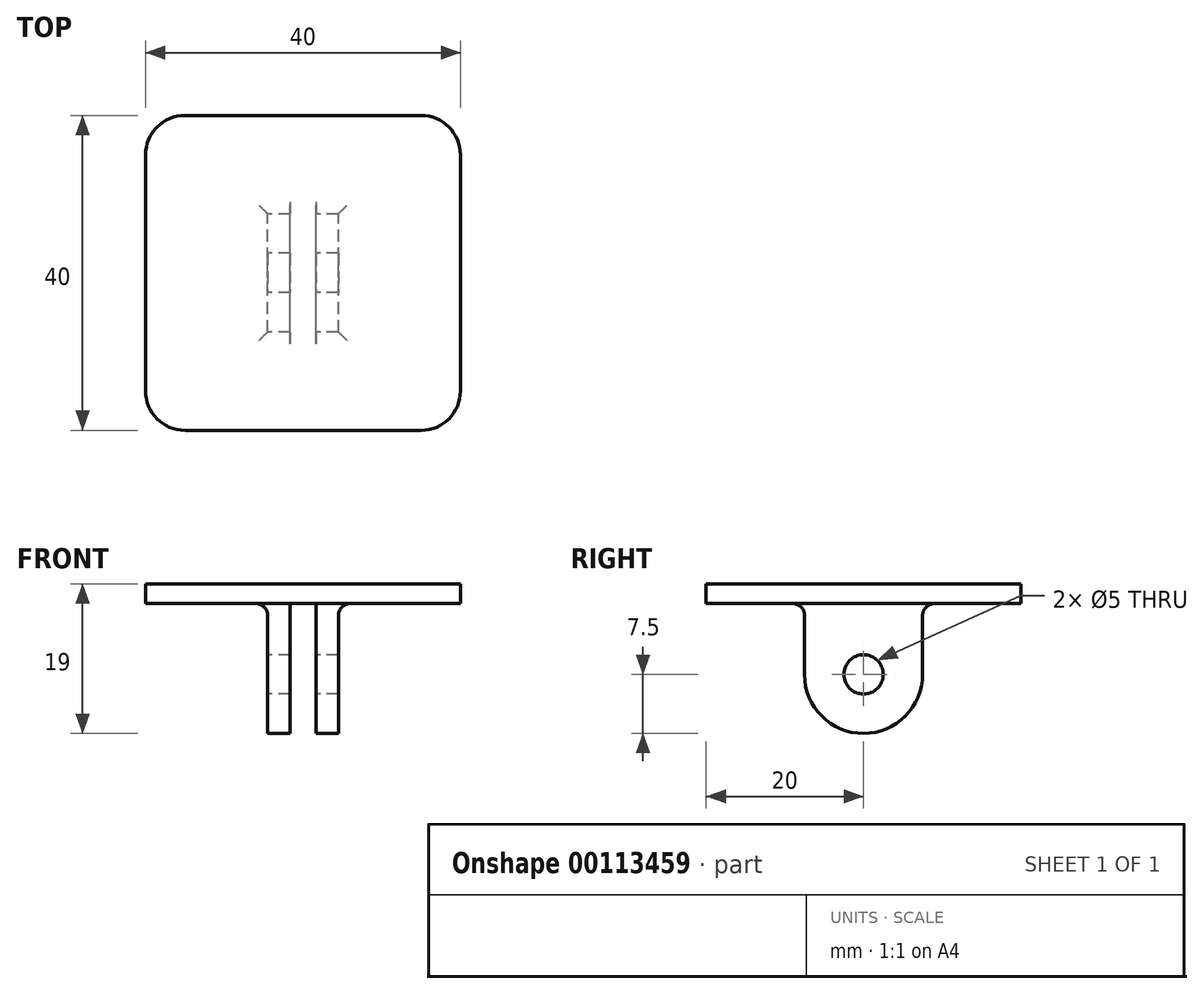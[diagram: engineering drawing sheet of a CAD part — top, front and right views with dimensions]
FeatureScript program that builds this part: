
annotation { "Feature Type Name" : "Feature", "Feature Type Description" : "" }
export const myFeature = defineFeature(function(context is Context, id is Id, definition is map)
    precondition{}
    {
        {
            var Q0;
            Q0=qCreatedBy(makeId("Right.planeOp"),FACE);
            var sketch = newSketch(context, id + "F0", { "sketchPlane" : qUnion([Q0])});
            skArc(sketch, "E0", {"start": v(-7.5, 0) * mm, "mid": v(0, -7.5) * mm, "end": v(7.5, 0) * mm});
            skLineSegment(sketch, "E1", {"start": v(-7.5, 0) * mm, "end": v(-7.5, 9) * mm});
            skLineSegment(sketch, "E2", {"start": v(-7.5, 9) * mm, "end": v(-20, 9) * mm});
            skLineSegment(sketch, "E3", {"start": v(-20, 9) * mm, "end": v(-20, 11.5) * mm});
            skLineSegment(sketch, "E4", {"start": v(-20, 11.5) * mm, "end": v(20, 11.5) * mm});
            skLineSegment(sketch, "E5", {"start": v(7.5, 0) * mm, "end": v(7.5, 9) * mm});
            skLineSegment(sketch, "E6", {"start": v(7.5, 9) * mm, "end": v(20, 9) * mm});
            skLineSegment(sketch, "E7", {"start": v(20, 9) * mm, "end": v(20, 11.5) * mm});
            skCircle(sketch, "E8", {"center": v(0, 0) * mm, "radius": 2.5 * mm});
            skLineSegment(sketch, "E9", {"start": v(-7.5, 9) * mm, "end": v(7.5, 9) * mm});
            skSolve(sketch);
        }
        {
            var Q0;
            Q0 = qSketchRegion(id + "F0", true);
            extrude(context, id + "F1", {"entities" : qUnion([Q0]), "endBound" : BoundingType.SYMMETRIC, "depth" : 9 * mm});
        }
        {
            var Q0;
            Q0=makeQuery(id+"F0.imprint","IMPRINT",FACE,{"disambiguationData":[TD([[makeQuery(id+"F0.imprint","IMPRINT",EDGE,{"derivedFrom":sQuery(id+"F0.wireOp",EDGE,"E2")}),-1.0]])]});
            extrude(context, id + "F2", {"entities" : qUnion([Q0]), "operationType" : NewBodyOperationType.ADD, "endBound" : BoundingType.SYMMETRIC, "depth" : 40 * mm});
        }
        {
            var Q0;
            {var subQ0=sQuery(id+"F0.wireOp",EDGE,"E6");var subQ1=sQuery(id+"F0.wireOp",EDGE,"E2");Q0=makeQuery(id+"F2.boolean.opBoolean","MERGE",FACE,{"derivedFrom":[makeQuery(id+"F1.opExtrude","SWEPT_FACE",FACE,{"disambiguationData":[OSD([subQ1])]}),makeQuery(id+"F1.opExtrude","SWEPT_FACE",FACE,{"disambiguationData":[OSD([subQ0])]}),makeQuery(id+"F2.opExtrude","SWEPT_FACE",FACE,{"disambiguationData":[OSD([subQ1,subQ0,sQuery(id+"F0.wireOp",EDGE,"E9")])]})]});}
            var sketch = newSketch(context, id + "F3", { "sketchPlane" : qUnion([Q0])});
            skLineSegment(sketch, "E10.bottom", {"start": v(1.63, 10) * mm, "end": v(-1.62, 10) * mm});
            skLineSegment(sketch, "E10.top", {"start": v(1.63, -10) * mm, "end": v(-1.63, -10) * mm});
            skLineSegment(sketch, "E10.left", {"start": v(1.63, 10) * mm, "end": v(1.63, -10) * mm});
            skLineSegment(sketch, "E10.right", {"start": v(-1.62, 10) * mm, "end": v(-1.63, -10) * mm});
            skPoint(sketch, "E10.middle", {"position": v(0, 0) * mm});
            skSolve(sketch);
        }
        {
            var Q0;
            Q0 = qSketchRegion(id + "F3", true);
            extrude(context, id + "F4", {"entities" : qUnion([Q0]), "operationType" : NewBodyOperationType.REMOVE, "depth" : 25 * mm});
        }
        {
            var Q0;
            {var subQ0=sQuery(id+"F0.wireOp",EDGE,"E6");var subQ1=sQuery(id+"F0.wireOp",EDGE,"E2");Q0=makeQuery(id+"F2.boolean.opBoolean","INTERSECT",EDGE,{"derivedFrom":[makeQuery(id+"F1.opExtrude","CAP_FACE",FACE,{"disambiguationData":[OSD([sQuery(id+"F0.wireOp",EDGE,"E0"),sQuery(id+"F0.wireOp",EDGE,"E1"),subQ1,sQuery(id+"F0.wireOp",EDGE,"E3"),sQuery(id+"F0.wireOp",EDGE,"E4"),sQuery(id+"F0.wireOp",EDGE,"E5"),subQ0,sQuery(id+"F0.wireOp",EDGE,"E7"),sQuery(id+"F0.wireOp",EDGE,"E8")])],"isStart":true}),makeQuery(id+"F2.opExtrude","SWEPT_FACE",FACE,{"disambiguationData":[OSD([subQ1,subQ0,sQuery(id+"F0.wireOp",EDGE,"E9")])]})]});}
            var Q1;
            {var subQ0=sQuery(id+"F0.wireOp",EDGE,"E6");var subQ1=sQuery(id+"F0.wireOp",EDGE,"E2");Q1=makeQuery(id+"F2.boolean.opBoolean","INTERSECT",EDGE,{"derivedFrom":[makeQuery(id+"F1.opExtrude","CAP_FACE",FACE,{"disambiguationData":[OSD([sQuery(id+"F0.wireOp",EDGE,"E0"),sQuery(id+"F0.wireOp",EDGE,"E1"),subQ1,sQuery(id+"F0.wireOp",EDGE,"E3"),sQuery(id+"F0.wireOp",EDGE,"E4"),sQuery(id+"F0.wireOp",EDGE,"E5"),subQ0,sQuery(id+"F0.wireOp",EDGE,"E7"),sQuery(id+"F0.wireOp",EDGE,"E8")])],"isStart":false}),makeQuery(id+"F2.opExtrude","SWEPT_FACE",FACE,{"disambiguationData":[OSD([subQ1,subQ0,sQuery(id+"F0.wireOp",EDGE,"E9")])]})]});}
            var Q2;
            {var subQ0=sQuery(id+"F0.wireOp",EDGE,"E6");var subQ1=sQuery(id+"F0.wireOp",EDGE,"E5");var subQ3=sQuery(id+"F0.wireOp",EDGE,"E9");var subQ4=sQuery(id+"F3.wireOp",EDGE,"E10.right");Q2=makeQuery(id+"F4.boolean.opBoolean","SPLIT",EDGE,{"disambiguationData":[TD([makeQuery(id+"F4.opExtrude","SWEPT_FACE",FACE,{"disambiguationData":[OSD([subQ4])]})])],"derivedFrom":makeQuery(id+"F1.opExtrude","SWEPT_EDGE",EDGE,{"disambiguationData":[OSD([subQ1,subQ0,subQ3])]})});}
            var Q3;
            {var subQ0=sQuery(id+"F0.wireOp",EDGE,"E5");var subQ2=sQuery(id+"F0.wireOp",EDGE,"E6");var subQ3=sQuery(id+"F0.wireOp",EDGE,"E9");var subQ4=sQuery(id+"F3.wireOp",EDGE,"E10.left");Q3=makeQuery(id+"F4.boolean.opBoolean","SPLIT",EDGE,{"disambiguationData":[TD([makeQuery(id+"F4.opExtrude","SWEPT_FACE",FACE,{"disambiguationData":[OSD([subQ4])]})])],"derivedFrom":makeQuery(id+"F1.opExtrude","SWEPT_EDGE",EDGE,{"disambiguationData":[OSD([subQ0,subQ2,subQ3])]})});}
            var Q4;
            {var subQ0=sQuery(id+"F0.wireOp",EDGE,"E2");var subQ2=sQuery(id+"F0.wireOp",EDGE,"E1");var subQ3=sQuery(id+"F0.wireOp",EDGE,"E9");var subQ4=sQuery(id+"F3.wireOp",EDGE,"E10.left");Q4=makeQuery(id+"F4.boolean.opBoolean","SPLIT",EDGE,{"disambiguationData":[TD([makeQuery(id+"F4.opExtrude","SWEPT_FACE",FACE,{"disambiguationData":[OSD([subQ4])]})])],"derivedFrom":makeQuery(id+"F1.opExtrude","SWEPT_EDGE",EDGE,{"disambiguationData":[OSD([subQ2,subQ0,subQ3])]})});}
            var Q5;
            {var subQ0=sQuery(id+"F0.wireOp",EDGE,"E2");var subQ2=sQuery(id+"F0.wireOp",EDGE,"E1");var subQ3=sQuery(id+"F3.wireOp",EDGE,"E10.right");var subQ4=sQuery(id+"F0.wireOp",EDGE,"E9");Q5=makeQuery(id+"F4.boolean.opBoolean","SPLIT",EDGE,{"disambiguationData":[TD([makeQuery(id+"F4.opExtrude","SWEPT_FACE",FACE,{"disambiguationData":[OSD([subQ3])]})])],"derivedFrom":makeQuery(id+"F1.opExtrude","SWEPT_EDGE",EDGE,{"disambiguationData":[OSD([subQ2,subQ0,subQ4])]})});}
            fillet(context, id + "F5", {"entities" : qUnion([Q0, Q1, Q2, Q3, Q4, Q5]), "radius" : 1.5 * mm, "allowEdgeOverflow" : false});
        }
        {
            var Q0;
            Q0=makeQuery(id+"F2.opExtrude","CAP_EDGE",EDGE,{"disambiguationData":[OSD([sQuery(id+"F0.wireOp",EDGE,"E3")])],"isStart":false});
            var Q1;
            Q1=makeQuery(id+"F2.opExtrude","CAP_EDGE",EDGE,{"disambiguationData":[OSD([sQuery(id+"F0.wireOp",EDGE,"E3")])],"isStart":true});
            var Q2;
            Q2=makeQuery(id+"F2.opExtrude","CAP_EDGE",EDGE,{"disambiguationData":[OSD([sQuery(id+"F0.wireOp",EDGE,"E7")])],"isStart":false});
            var Q3;
            Q3=makeQuery(id+"F2.opExtrude","CAP_EDGE",EDGE,{"disambiguationData":[OSD([sQuery(id+"F0.wireOp",EDGE,"E7")])],"isStart":true});
            fillet(context, id + "F6", {"entities" : qUnion([Q0, Q1, Q2, Q3]), "radius" : 5 * mm, "allowEdgeOverflow" : false});
        }
    });
